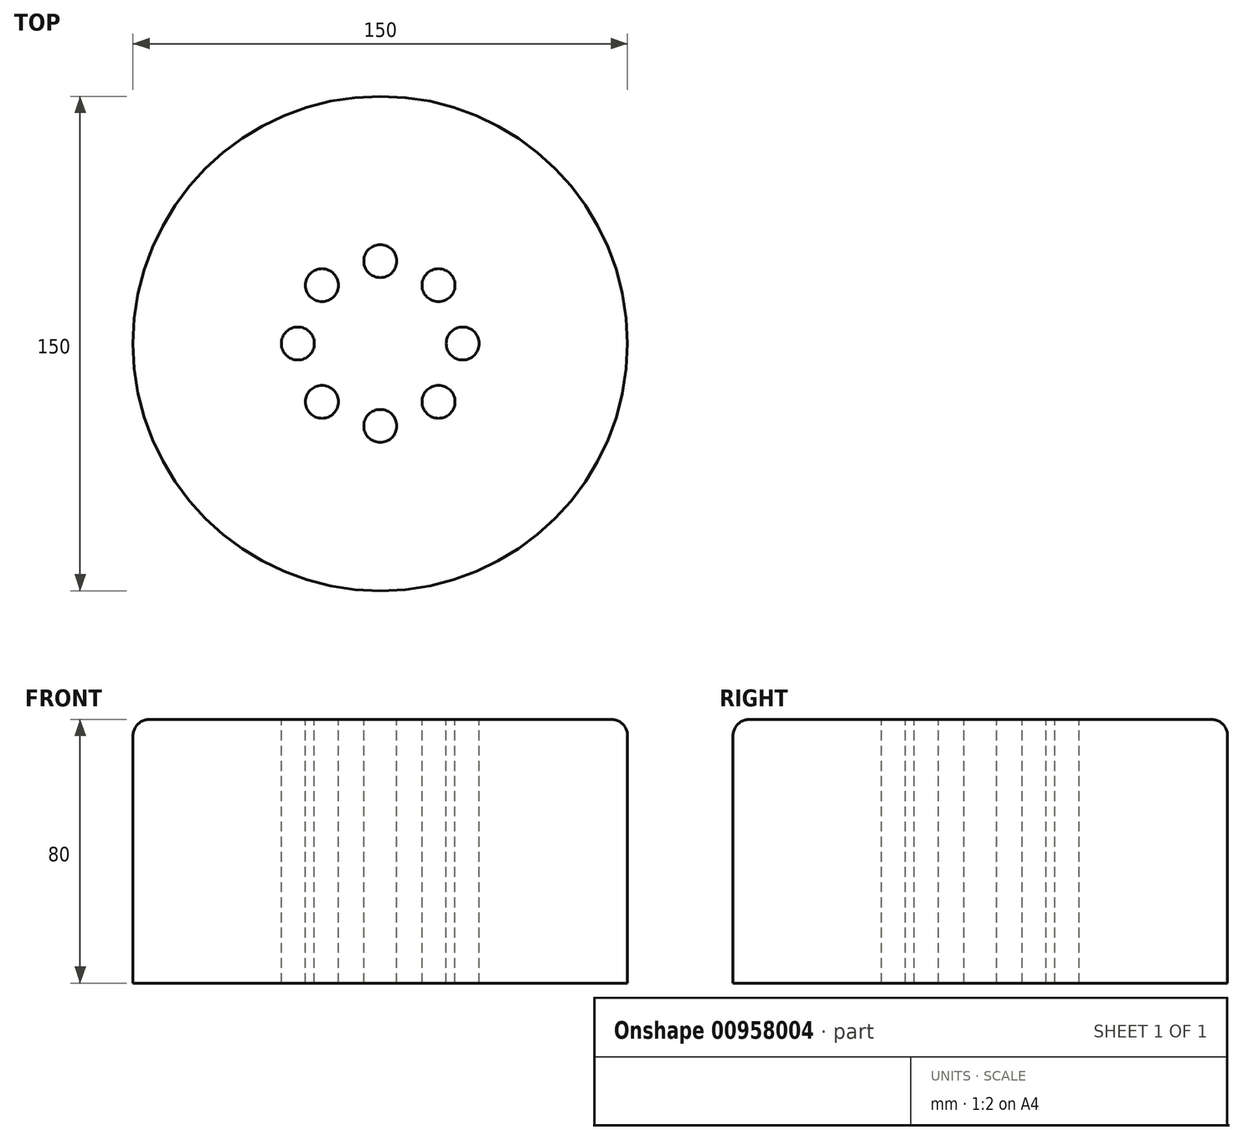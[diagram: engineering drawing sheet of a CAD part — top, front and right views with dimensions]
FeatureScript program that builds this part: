
annotation { "Feature Type Name" : "Feature", "Feature Type Description" : "" }
export const myFeature = defineFeature(function(context is Context, id is Id, definition is map)
    precondition{}
    {
        {
            var Q0;
            Q0=qCreatedBy(makeId("Top.planeOp"),FACE);
            var sketch = newSketch(context, id + "F0", { "sketchPlane" : qUnion([Q0])});
            skCircle(sketch, "E0", {"center": v(0, 0) * mm, "radius": 75 * mm});
            skSolve(sketch);
        }
        {
            var Q0;
            Q0=makeQuery(id+"F0.imprint","IMPRINT",FACE,{"disambiguationData":[TD([[makeQuery(id+"F0.imprint","IMPRINT",EDGE,{"derivedFrom":sQuery(id+"F0.wireOp",EDGE,"E0")}),1.0]])]});
            extrude(context, id + "F1", {"entities" : qUnion([Q0]), "depth" : 80 * mm, "offsetDistance" : 25.4 * mm});
        }
        {
            var Q0;
            Q0=makeQuery(id+"F1.opExtrude","CAP_EDGE",EDGE,{"disambiguationData":[OSD([sQuery(id+"F0.wireOp",EDGE,"E0")])],"isStart":false});
            fillet(context, id + "F2", {"entities" : qUnion([Q0]), "radius" : 5 * mm, "tangentPropagation" : true, "allowEdgeOverflow" : false});
        }
        {
            var Q0;
            Q0=makeQuery(id+"F1.opExtrude","CAP_FACE",FACE,{"disambiguationData":[OSD([sQuery(id+"F0.wireOp",EDGE,"E0")])],"isStart":false});
            var sketch = newSketch(context, id + "F3", { "sketchPlane" : qUnion([Q0])});
            skCircle(sketch, "E1", {"center": v(0, 25) * mm, "radius": 5 * mm});
            skCircle(sketch, "E2.1.0", {"center": v(-17.68, 17.68) * mm, "radius": 5 * mm});
            skCircle(sketch, "E2.2.0", {"center": v(-25, 0) * mm, "radius": 5 * mm});
            skCircle(sketch, "E2.3.0", {"center": v(-17.68, -17.68) * mm, "radius": 5 * mm});
            skCircle(sketch, "E2.4.0", {"center": v(0, -25) * mm, "radius": 5 * mm});
            skCircle(sketch, "E2.5.0", {"center": v(17.68, -17.68) * mm, "radius": 5 * mm});
            skCircle(sketch, "E2.6.0", {"center": v(25, 0) * mm, "radius": 5 * mm});
            skCircle(sketch, "E2.7.0", {"center": v(17.68, 17.68) * mm, "radius": 5 * mm});
            skPoint(sketch, "E2.center", {"position": v(0, 0) * mm});
            skSolve(sketch);
        }
        {
            var Q0;
            Q0=makeQuery(id+"F3.imprint","IMPRINT",FACE,{"disambiguationData":[TD([[makeQuery(id+"F3.imprint","IMPRINT",EDGE,{"derivedFrom":sQuery(id+"F3.wireOp",EDGE,"E2.1.0")}),1.0]])]});
            var Q1;
            Q1=makeQuery(id+"F3.imprint","IMPRINT",FACE,{"disambiguationData":[TD([[makeQuery(id+"F3.imprint","IMPRINT",EDGE,{"derivedFrom":sQuery(id+"F3.wireOp",EDGE,"E1")}),1.0]])]});
            var Q2;
            Q2=makeQuery(id+"F3.imprint","IMPRINT",FACE,{"disambiguationData":[TD([[makeQuery(id+"F3.imprint","IMPRINT",EDGE,{"derivedFrom":sQuery(id+"F3.wireOp",EDGE,"E2.7.0")}),1.0]])]});
            var Q3;
            Q3=makeQuery(id+"F3.imprint","IMPRINT",FACE,{"disambiguationData":[TD([[makeQuery(id+"F3.imprint","IMPRINT",EDGE,{"derivedFrom":sQuery(id+"F3.wireOp",EDGE,"E2.6.0")}),1.0]])]});
            var Q4;
            Q4=makeQuery(id+"F3.imprint","IMPRINT",FACE,{"disambiguationData":[TD([[makeQuery(id+"F3.imprint","IMPRINT",EDGE,{"derivedFrom":sQuery(id+"F3.wireOp",EDGE,"E2.4.0")}),1.0]])]});
            var Q5;
            Q5=makeQuery(id+"F3.imprint","IMPRINT",FACE,{"disambiguationData":[TD([[makeQuery(id+"F3.imprint","IMPRINT",EDGE,{"derivedFrom":sQuery(id+"F3.wireOp",EDGE,"E2.5.0")}),1.0]])]});
            var Q6;
            Q6=makeQuery(id+"F3.imprint","IMPRINT",FACE,{"disambiguationData":[TD([[makeQuery(id+"F3.imprint","IMPRINT",EDGE,{"derivedFrom":sQuery(id+"F3.wireOp",EDGE,"E2.3.0")}),1.0]])]});
            var Q7;
            Q7=makeQuery(id+"F3.imprint","IMPRINT",FACE,{"disambiguationData":[TD([[makeQuery(id+"F3.imprint","IMPRINT",EDGE,{"derivedFrom":sQuery(id+"F3.wireOp",EDGE,"E2.2.0")}),1.0]])]});
            var Q8;
            Q8=makeQuery(id+"F1.opExtrude","CAP_FACE",FACE,{"disambiguationData":[OSD([sQuery(id+"F0.wireOp",EDGE,"E0")])],"isStart":true});
            extrude(context, id + "F4", {"entities" : qUnion([Q0, Q1, Q2, Q3, Q4, Q5, Q6, Q7]), "operationType" : NewBodyOperationType.REMOVE, "endBound" : BoundingType.UP_TO_SURFACE, "oppositeDirection" : true, "depth" : 25.4 * mm, "endBoundEntityFace" : qUnion([Q8]), "offsetDistance" : 25.4 * mm});
        }
    });
